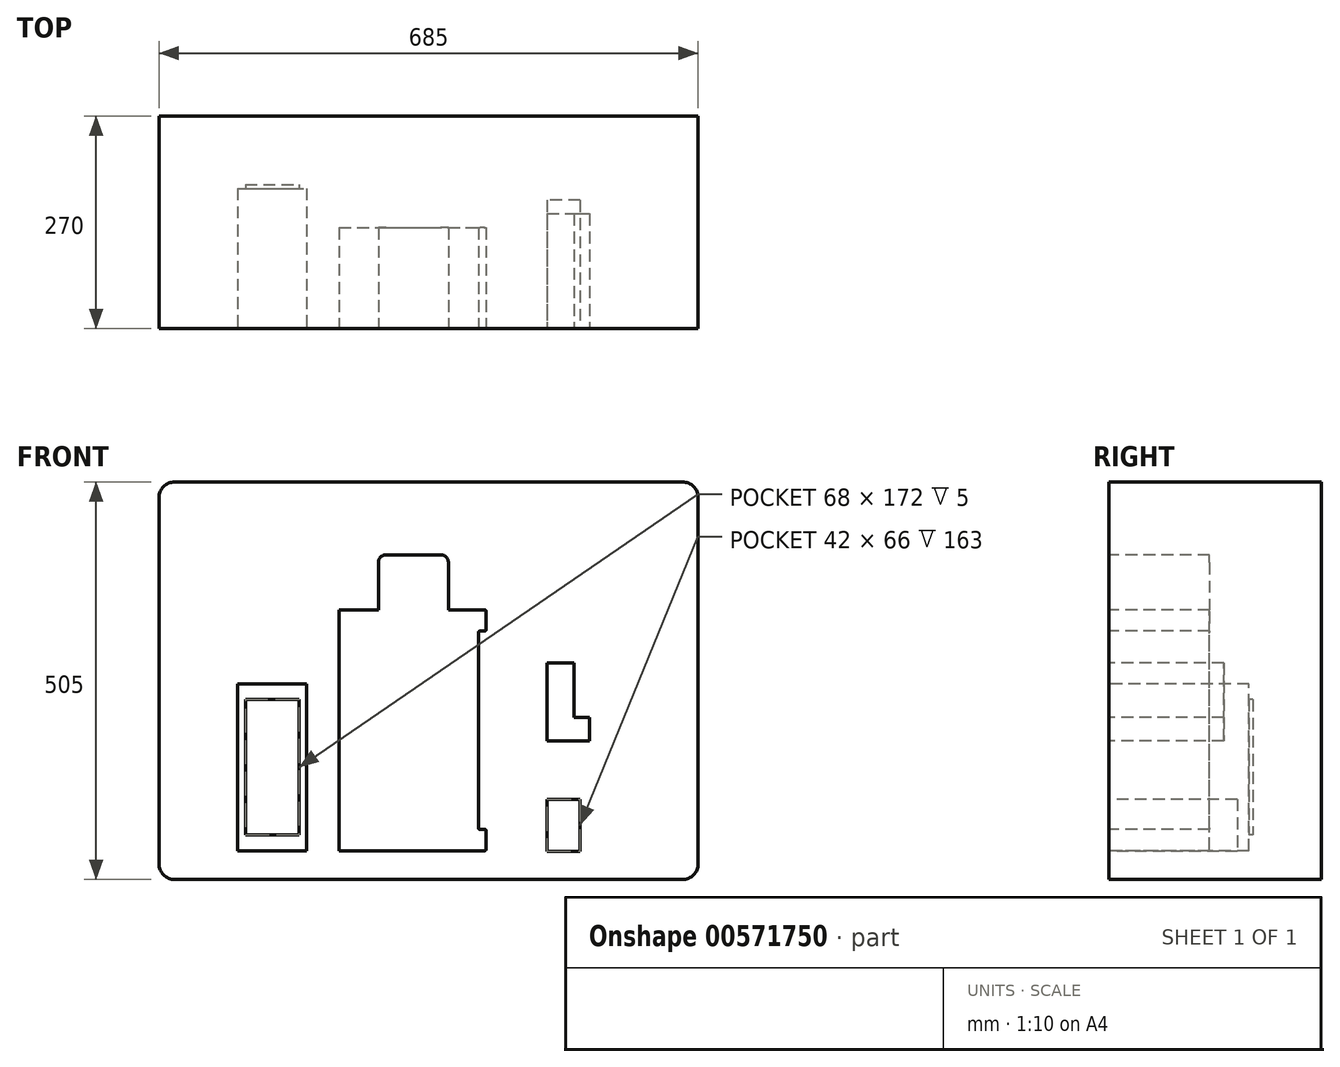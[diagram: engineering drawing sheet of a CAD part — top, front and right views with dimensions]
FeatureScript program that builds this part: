
annotation { "Feature Type Name" : "Feature", "Feature Type Description" : "" }
export const myFeature = defineFeature(function(context is Context, id is Id, definition is map)
    precondition{}
    {
        {
            var Q0;
            Q0=qCreatedBy(makeId("Front.planeOp"),FACE);
            var sketch = newSketch(context, id + "F0", { "sketchPlane" : qUnion([Q0])});
            skLineSegment(sketch, "E0.bottom", {"start": v(-665, 505) * mm, "end": v(-20, 505) * mm});
            skLineSegment(sketch, "E0.top", {"start": v(-665, 0) * mm, "end": v(-20, 0) * mm});
            skLineSegment(sketch, "E0.left", {"start": v(-685, 485) * mm, "end": v(-685, 20) * mm});
            skLineSegment(sketch, "E0.right", {"start": v(0, 485) * mm, "end": v(0, 20) * mm});
            skPoint(sketch, "E1.visualSharp", {"position": v(-685, 505) * mm});
            skArc(sketch, "E1.filletArc", {"start": v(-665, 505) * mm, "mid": v(-679.14, 499.14) * mm, "end": v(-685, 485) * mm});
            skPoint(sketch, "E2.visualSharp", {"position": v(-685, 0) * mm});
            skArc(sketch, "E2.filletArc", {"start": v(-685, 20) * mm, "mid": v(-679.14, 5.86) * mm, "end": v(-665, 0) * mm});
            skPoint(sketch, "E3.visualSharp", {"position": v(0, 0) * mm});
            skArc(sketch, "E3.filletArc", {"start": v(-20, 0) * mm, "mid": v(-5.86, 5.86) * mm, "end": v(0, 20) * mm});
            skPoint(sketch, "E4.visualSharp", {"position": v(0, 505) * mm});
            skArc(sketch, "E4.filletArc", {"start": v(0, 485) * mm, "mid": v(-5.86, 499.14) * mm, "end": v(-20, 505) * mm});
            skSolve(sketch);
        }
        {
            var Q0;
            Q0=makeQuery(id+"F0.imprint","IMPRINT",FACE,{"disambiguationData":[TD([[makeQuery(id+"F0.imprint","IMPRINT",EDGE,{"derivedFrom":sQuery(id+"F0.wireOp",EDGE,"E0.bottom")}),-1.0]])]});
            extrude(context, id + "F1", {"entities" : qUnion([Q0]), "oppositeDirection" : true, "depth" : 270 * mm, "offsetDistance" : 25 * mm});
        }
        {
            var Q0;
            Q0=makeQuery(id+"F1.opExtrude","CAP_FACE",FACE,{"disambiguationData":[OSD([sQuery(id+"F0.wireOp",EDGE,"E0.bottom"),sQuery(id+"F0.wireOp",EDGE,"E0.top"),sQuery(id+"F0.wireOp",EDGE,"E0.left"),sQuery(id+"F0.wireOp",EDGE,"E0.right")])],"isStart":true});
            var sketch = newSketch(context, id + "F2", { "sketchPlane" : qUnion([Q0])});
            skLineSegment(sketch, "E5.bottom", {"start": v(-585.25, 36.6) * mm, "end": v(-497.25, 36.6) * mm});
            skLineSegment(sketch, "E5.top", {"start": v(-585.25, 248.6) * mm, "end": v(-497.25, 248.6) * mm});
            skLineSegment(sketch, "E5.left", {"start": v(-585.25, 36.6) * mm, "end": v(-585.25, 248.6) * mm});
            skLineSegment(sketch, "E5.right", {"start": v(-497.25, 36.6) * mm, "end": v(-497.25, 248.6) * mm});
            skSolve(sketch);
        }
        {
            var Q0;
            Q0 = qSketchRegion(id + "F2", true);
            extrude(context, id + "F3", {"entities" : qUnion([Q0]), "operationType" : NewBodyOperationType.REMOVE, "oppositeDirection" : true, "depth" : 178 * mm, "offsetDistance" : 25 * mm});
        }
        {
            var Q0;
            Q0=makeQuery(id+"F3.boolean.opBoolean","COPY",FACE,{"derivedFrom":makeQuery(id+"F3.opExtrude","CAP_FACE",FACE,{"disambiguationData":[OSD([sQuery(id+"F2.wireOp",EDGE,"E5.bottom"),sQuery(id+"F2.wireOp",EDGE,"E5.top"),sQuery(id+"F2.wireOp",EDGE,"E5.left"),sQuery(id+"F2.wireOp",EDGE,"E5.right")])],"isStart":false})});
            var sketch = newSketch(context, id + "F4", { "sketchPlane" : qUnion([Q0])});
            skLineSegment(sketch, "E6.bottom", {"start": v(-575.25, 228.6) * mm, "end": v(-507.25, 228.6) * mm});
            skLineSegment(sketch, "E6.top", {"start": v(-575.25, 56.6) * mm, "end": v(-507.25, 56.6) * mm});
            skLineSegment(sketch, "E6.left", {"start": v(-575.25, 228.6) * mm, "end": v(-575.25, 56.6) * mm});
            skLineSegment(sketch, "E6.right", {"start": v(-507.25, 228.6) * mm, "end": v(-507.25, 56.6) * mm});
            skSolve(sketch);
        }
        {
            var Q0;
            Q0=makeQuery(id+"F4.imprint","IMPRINT",FACE,{"disambiguationData":[TD([[makeQuery(id+"F4.imprint","IMPRINT",EDGE,{"derivedFrom":sQuery(id+"F4.wireOp",EDGE,"E6.bottom")}),-1.0]])]});
            extrude(context, id + "F5", {"entities" : qUnion([Q0]), "operationType" : NewBodyOperationType.REMOVE, "oppositeDirection" : true, "depth" : 5 * mm, "offsetDistance" : 25 * mm});
        }
        {
            var Q0;
            Q0=makeQuery(id+"F1.opExtrude","CAP_FACE",FACE,{"disambiguationData":[OSD([sQuery(id+"F0.wireOp",EDGE,"E0.bottom"),sQuery(id+"F0.wireOp",EDGE,"E0.top"),sQuery(id+"F0.wireOp",EDGE,"E0.left"),sQuery(id+"F0.wireOp",EDGE,"E0.right")])],"isStart":true});
            var sketch = newSketch(context, id + "F6", { "sketchPlane" : qUnion([Q0])});
            skLineSegment(sketch, "E7.bottom", {"start": v(-456.3, 36.6) * mm, "end": v(-279.3, 36.6) * mm});
            skLineSegment(sketch, "E7.top", {"start": v(-456.3, 342.6) * mm, "end": v(-406.3, 342.6) * mm});
            skLineSegment(sketch, "E7.left", {"start": v(-456.3, 36.6) * mm, "end": v(-456.3, 342.6) * mm});
            skLineSegment(sketch, "E8", {"start": v(-271.3, 342.6) * mm, "end": v(-271.3, 342.6) * mm});
            skLineSegment(sketch, "E9", {"start": v(-269.3, 340.6) * mm, "end": v(-269.3, 317.6) * mm});
            skLineSegment(sketch, "E10", {"start": v(-271.3, 315.6) * mm, "end": v(-277.3, 315.6) * mm});
            skPoint(sketch, "E11.visualSharp", {"position": v(-269.3, 342.6) * mm});
            skArc(sketch, "E11.filletArc", {"start": v(-269.3, 340.6) * mm, "mid": v(-269.88, 342) * mm, "end": v(-271.3, 342.6) * mm});
            skPoint(sketch, "E12.visualSharp", {"position": v(-269.3, 315.6) * mm});
            skArc(sketch, "E12.filletArc", {"start": v(-271.3, 315.6) * mm, "mid": v(-269.88, 316.18) * mm, "end": v(-269.3, 317.6) * mm});
            skArc(sketch, "E13.filletArc", {"start": v(-277.3, 315.6) * mm, "mid": v(-278.71, 315) * mm, "end": v(-279.3, 313.6) * mm});
            skLineSegment(sketch, "E14", {"start": v(-279.3, 36.6) * mm, "end": v(-271.3, 36.6) * mm});
            skLineSegment(sketch, "E15", {"start": v(-269.3, 38.6) * mm, "end": v(-269.3, 61.6) * mm});
            skLineSegment(sketch, "E16", {"start": v(-271.3, 63.6) * mm, "end": v(-277.3, 63.6) * mm});
            skLineSegment(sketch, "E17", {"start": v(-279.3, 63.6) * mm, "end": v(-279.3, 63.6) * mm});
            skLineSegment(sketch, "E18", {"start": v(-279.3, 65.6) * mm, "end": v(-279.3, 313.6) * mm});
            skPoint(sketch, "E19.visualSharp", {"position": v(-269.3, 36.6) * mm});
            skArc(sketch, "E19.filletArc", {"start": v(-271.3, 36.6) * mm, "mid": v(-269.88, 37.18) * mm, "end": v(-269.3, 38.6) * mm});
            skPoint(sketch, "E20.visualSharp", {"position": v(-269.3, 63.6) * mm});
            skArc(sketch, "E20.filletArc", {"start": v(-269.3, 61.6) * mm, "mid": v(-269.88, 63) * mm, "end": v(-271.3, 63.6) * mm});
            skPoint(sketch, "E21.visualSharp", {"position": v(-279.3, 63.6) * mm});
            skArc(sketch, "E21.filletArc", {"start": v(-279.3, 65.6) * mm, "mid": v(-278.71, 64.18) * mm, "end": v(-277.3, 63.6) * mm});
            skLineSegment(sketch, "E22", {"start": v(-406.3, 342.6) * mm, "end": v(-406.3, 402.6) * mm});
            skLineSegment(sketch, "E23", {"start": v(-396.3, 412.6) * mm, "end": v(-327.3, 412.6) * mm});
            skLineSegment(sketch, "E24", {"start": v(-317.3, 402.6) * mm, "end": v(-317.3, 342.6) * mm});
            skPoint(sketch, "E25.visualSharp", {"position": v(-406.3, 412.6) * mm});
            skArc(sketch, "E25.filletArc", {"start": v(-396.3, 412.6) * mm, "mid": v(-403.37, 409.67) * mm, "end": v(-406.3, 402.6) * mm});
            skPoint(sketch, "E26.visualSharp", {"position": v(-317.3, 412.6) * mm});
            skArc(sketch, "E26.filletArc", {"start": v(-317.3, 402.6) * mm, "mid": v(-320.23, 409.67) * mm, "end": v(-327.3, 412.6) * mm});
            skLineSegment(sketch, "E27", {"start": v(-317.3, 342.6) * mm, "end": v(-271.3, 342.6) * mm});
            skSolve(sketch);
        }
        {
            var Q0;
            Q0=makeQuery(id+"F6.imprint","IMPRINT",FACE,{"disambiguationData":[TD([[makeQuery(id+"F6.imprint","IMPRINT",EDGE,{"derivedFrom":sQuery(id+"F6.wireOp",EDGE,"E7.bottom")}),1.0]])]});
            extrude(context, id + "F7", {"entities" : qUnion([Q0]), "operationType" : NewBodyOperationType.REMOVE, "oppositeDirection" : true, "depth" : 128 * mm, "offsetDistance" : 25 * mm});
        }
        {
            var Q0;
            Q0=makeQuery(id+"F1.opExtrude","CAP_FACE",FACE,{"disambiguationData":[OSD([sQuery(id+"F0.wireOp",EDGE,"E0.bottom"),sQuery(id+"F0.wireOp",EDGE,"E0.top"),sQuery(id+"F0.wireOp",EDGE,"E0.left"),sQuery(id+"F0.wireOp",EDGE,"E0.right"),sQuery(id+"F0.wireOp",EDGE,"E1.filletArc"),sQuery(id+"F0.wireOp",EDGE,"E2.filletArc"),sQuery(id+"F0.wireOp",EDGE,"E3.filletArc"),sQuery(id+"F0.wireOp",EDGE,"E4.filletArc")])],"isStart":true});
            var sketch = newSketch(context, id + "F8", { "sketchPlane" : qUnion([Q0])});
            skLineSegment(sketch, "E28.bottom", {"start": v(-150, 101.9) * mm, "end": v(-192, 101.9) * mm});
            skLineSegment(sketch, "E28.top", {"start": v(-150, 35.9) * mm, "end": v(-192, 35.9) * mm});
            skLineSegment(sketch, "E28.left", {"start": v(-150, 101.9) * mm, "end": v(-150, 35.9) * mm});
            skLineSegment(sketch, "E28.right", {"start": v(-192, 101.9) * mm, "end": v(-192, 35.9) * mm});
            skSolve(sketch);
        }
        {
            var Q0;
            Q0=makeQuery(id+"F8.imprint","IMPRINT",FACE,{"disambiguationData":[TD([[makeQuery(id+"F8.imprint","IMPRINT",EDGE,{"derivedFrom":sQuery(id+"F8.wireOp",EDGE,"E28.bottom")}),1.0]])]});
            extrude(context, id + "F9", {"entities" : qUnion([Q0]), "operationType" : NewBodyOperationType.REMOVE, "oppositeDirection" : true, "depth" : 163 * mm, "offsetDistance" : 25 * mm});
        }
        {
            var Q0;
            Q0=makeQuery(id+"F1.opExtrude","CAP_FACE",FACE,{"disambiguationData":[OSD([sQuery(id+"F0.wireOp",EDGE,"E0.bottom"),sQuery(id+"F0.wireOp",EDGE,"E0.top"),sQuery(id+"F0.wireOp",EDGE,"E0.left"),sQuery(id+"F0.wireOp",EDGE,"E0.right"),sQuery(id+"F0.wireOp",EDGE,"E1.filletArc"),sQuery(id+"F0.wireOp",EDGE,"E2.filletArc"),sQuery(id+"F0.wireOp",EDGE,"E3.filletArc"),sQuery(id+"F0.wireOp",EDGE,"E4.filletArc")])],"isStart":true});
            var sketch = newSketch(context, id + "F10", { "sketchPlane" : qUnion([Q0])});
            skLineSegment(sketch, "E29", {"start": v(-192, 176.06) * mm, "end": v(-192, 275.06) * mm});
            skLineSegment(sketch, "E30", {"start": v(-192, 275.06) * mm, "end": v(-158, 275.06) * mm});
            skLineSegment(sketch, "E31", {"start": v(-158, 275.06) * mm, "end": v(-158, 206.06) * mm});
            skLineSegment(sketch, "E32", {"start": v(-158, 206.06) * mm, "end": v(-138, 206.06) * mm});
            skLineSegment(sketch, "E33", {"start": v(-192, 176.06) * mm, "end": v(-138, 176.06) * mm});
            skLineSegment(sketch, "E34", {"start": v(-138, 206.06) * mm, "end": v(-138, 176.06) * mm});
            skSolve(sketch);
        }
        {
            var Q0;
            Q0=makeQuery(id+"F10.imprint","IMPRINT",FACE,{"disambiguationData":[TD([[makeQuery(id+"F10.imprint","IMPRINT",EDGE,{"derivedFrom":sQuery(id+"F10.wireOp",EDGE,"E29")}),-1.0]])]});
            extrude(context, id + "F11", {"entities" : qUnion([Q0]), "operationType" : NewBodyOperationType.REMOVE, "oppositeDirection" : true, "depth" : 146 * mm, "offsetDistance" : 25 * mm});
        }
    });
